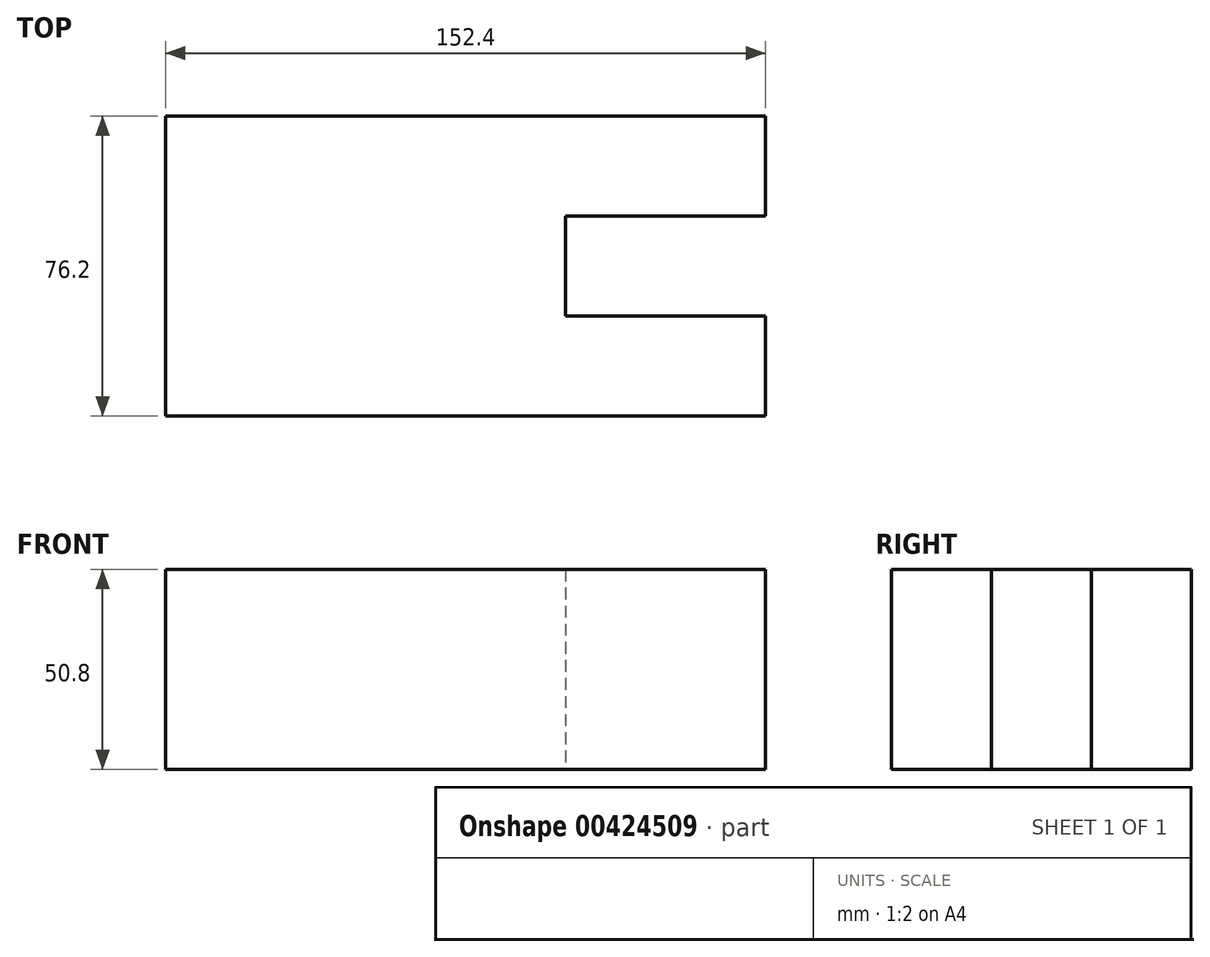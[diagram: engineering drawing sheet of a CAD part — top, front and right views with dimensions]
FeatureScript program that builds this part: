
annotation { "Feature Type Name" : "Feature", "Feature Type Description" : "" }
export const myFeature = defineFeature(function(context is Context, id is Id, definition is map)
    precondition{}
    {
        {
            var Q0;
            Q0=qCreatedBy(makeId("Front.planeOp"),FACE);
            var sketch = newSketch(context, id + "F0", { "sketchPlane" : qUnion([Q0])});
            skLineSegment(sketch, "E0", {"start": v(0, 0) * mm, "end": v(152.4, 0) * mm});
            skLineSegment(sketch, "E1", {"start": v(0, 0) * mm, "end": v(0, 50.8) * mm});
            skLineSegment(sketch, "E2", {"start": v(0, 50.8) * mm, "end": v(152.4, 50.8) * mm});
            skLineSegment(sketch, "E3", {"start": v(152.4, 50.8) * mm, "end": v(152.4, 0) * mm});
            skSolve(sketch);
        }
        {
            var Q0;
            Q0=makeQuery(id+"F0.imprint","IMPRINT",FACE,{"disambiguationData":[TD([[makeQuery(id+"F0.imprint","IMPRINT",EDGE,{"derivedFrom":sQuery(id+"F0.wireOp",EDGE,"E0")}),1.0]])]});
            extrude(context, id + "F1", {"entities" : qUnion([Q0]), "depth" : 76.2 * mm});
        }
        {
            var Q0;
            Q0=makeQuery(id+"F1.opExtrude","SWEPT_FACE",FACE,{"disambiguationData":[OSD([sQuery(id+"F0.wireOp",EDGE,"E3")])]});
            var sketch = newSketch(context, id + "F2", { "sketchPlane" : qUnion([Q0])});
            skLineSegment(sketch, "E4", {"start": v(-38.1, 50.8) * mm, "end": v(-50.8, 50.8) * mm});
            skLineSegment(sketch, "E5", {"start": v(-38.1, 50.8) * mm, "end": v(-25.4, 50.8) * mm});
            skLineSegment(sketch, "E6", {"start": v(-25.4, 50.8) * mm, "end": v(-25.4, 0) * mm});
            skLineSegment(sketch, "E7", {"start": v(-25.4, 0) * mm, "end": v(-50.8, 0) * mm});
            skLineSegment(sketch, "E8", {"start": v(-50.8, 50.8) * mm, "end": v(-50.8, 0) * mm});
            skSolve(sketch);
        }
        {
            var Q0;
            Q0 = qSketchRegion(id + "F2", true);
            extrude(context, id + "F3", {"entities" : qUnion([Q0]), "operationType" : NewBodyOperationType.REMOVE, "oppositeDirection" : true, "depth" : 50.8 * mm});
        }
    });
